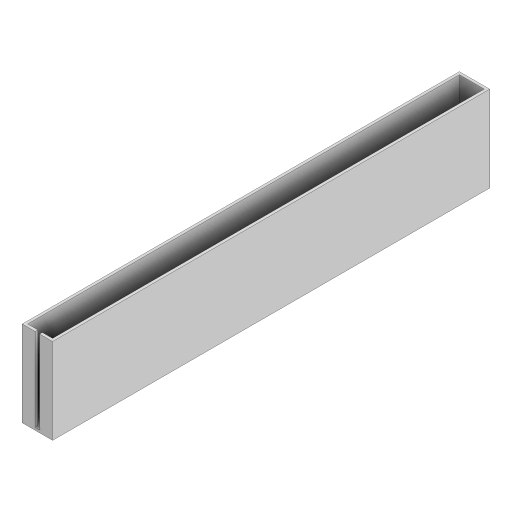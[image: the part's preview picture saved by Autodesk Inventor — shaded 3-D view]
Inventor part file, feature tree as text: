
AUTODESK INVENTOR PART (.ipt)
format: ipt  version: 2024.2 (Build 282272000, 272)  size: 118,784 bytes
history: native  units: in
note: dims shown in document units (in); Inventor stores cm internally (conversion verified against a paired STEP export)
features: extrude x2, sketch x2, shell x1
ambient origin geometry x8: Origin, YZ Plane, XZ Plane, XY Plane, X Axis, Y Axis, Z Axis, Center Point
bodies: Solid1 (feature_tree)
feature tree (5):
  extrude  "Extrusion1"  Depth=10.2075in
  shell  "Shell1"  Thickness=2.0in
  extrude  "Extrusion2"  TaperAngle=0.0deg  [1 undecoded]
  sketch  "Sketch1"  dims[d0=0.7075in d1=10.2075in d2=2.0in d3=0.0in]
  sketch  "Sketch2"  dims[d4=0.0625in d5=0.0in d6=0.24in d7=0.24in d8=0.0625in d9=0.0in]
note: 1 required parameter value undecoded (feature->parameter linkage not recoverable at this tier; creation-order binding heuristic only, values carry confidence <= 0.55)
